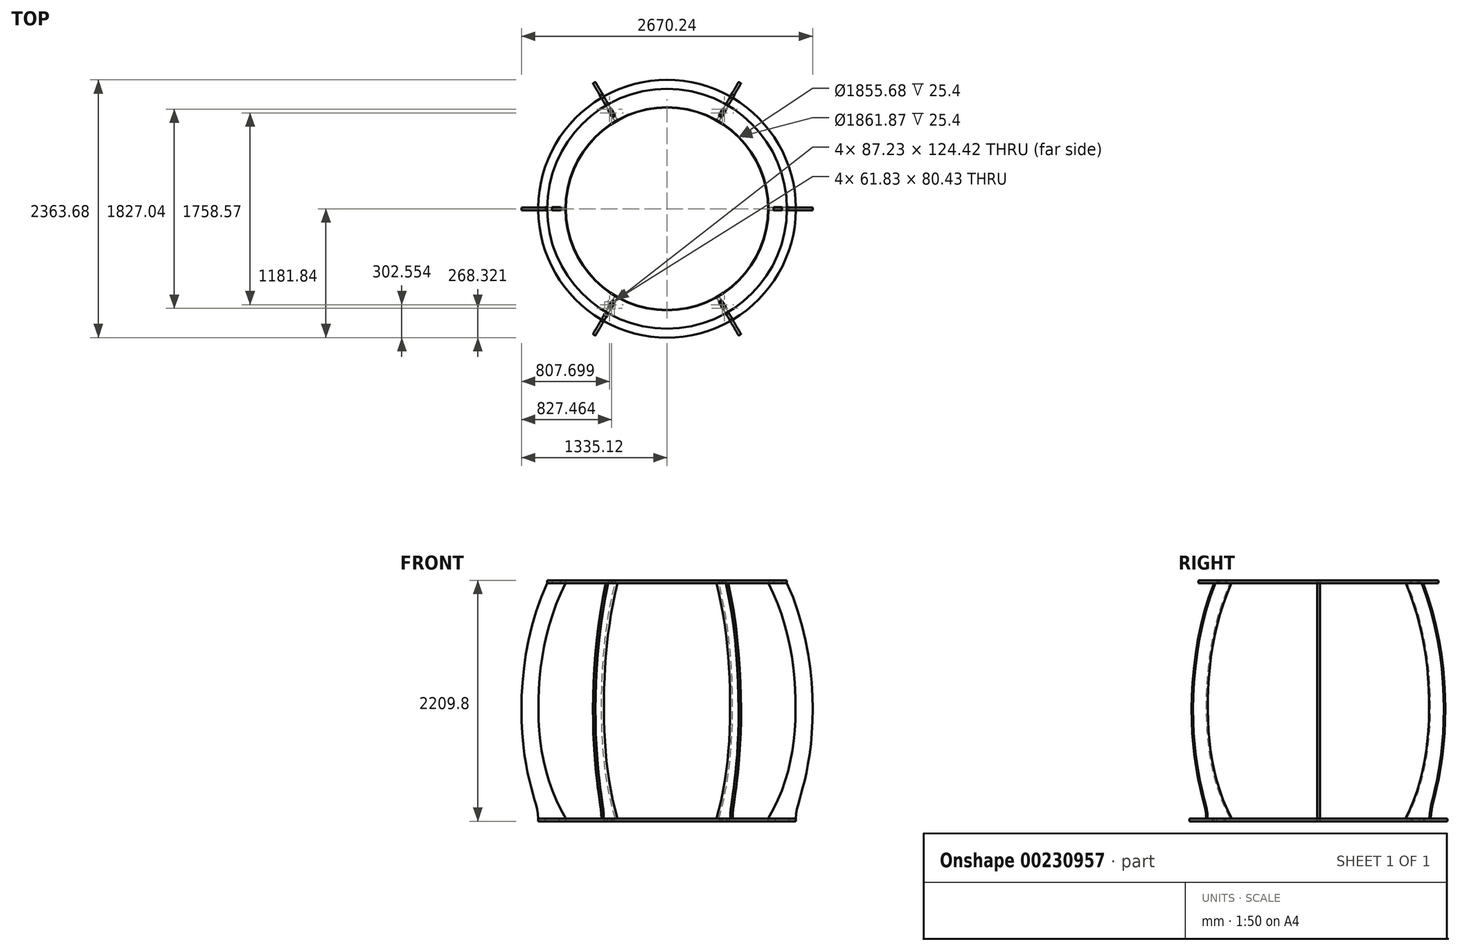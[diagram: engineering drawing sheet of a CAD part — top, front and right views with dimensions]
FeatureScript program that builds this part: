
annotation { "Feature Type Name" : "Feature", "Feature Type Description" : "" }
export const myFeature = defineFeature(function(context is Context, id is Id, definition is map)
    precondition{}
    {
        {
            var Q0;
            Q0=qCreatedBy(makeId("Front.planeOp"),FACE);
            var sketch = newSketch(context, id + "F0", { "sketchPlane" : qUnion([Q0])});
            skLineSegment(sketch, "E0", {"start": v(-1181.84, -1150.9) * mm, "end": v(-927.84, -1150.9) * mm});
            skFitSpline(sketch, "E1", {"points": [v(0, 1953.34) * mm, v(-1100.72, 1005.82) * mm, v(-1321.31, -446.03) * mm, v(-1216.83, -971.67) * mm, v(-1181.84, -1150.9) * mm], "startDerivative": vector(-4000.43, 5.06) * mm, "endDerivative": vector(0, -1489.55) * mm});
            skLineSegment(sketch, "E2", {"start": v(-1099.69, 1008.1) * mm, "end": v(-930.94, 1008.1) * mm});
            skLineSegment(sketch, "E3", {"start": v(-1181.84, -1150.9) * mm, "end": v(-1181.84, -1354.1) * mm});
            skLineSegment(sketch, "E4", {"start": v(-1181.84, -1354.1) * mm, "end": v(-877.04, -1354.1) * mm});
            skLineSegment(sketch, "E5", {"start": v(-877.04, -1354.1) * mm, "end": v(-877.04, -1252.5) * mm});
            skLineSegment(sketch, "E6", {"start": v(-877.04, -1252.5) * mm, "end": v(-927.84, -1252.5) * mm});
            skLineSegment(sketch, "E7", {"start": v(-927.84, -1252.5) * mm, "end": v(-927.84, -1150.9) * mm});
            skFitSpline(sketch, "E8.trimOffspring", {"points": [v(0, -1757.92) * mm, v(-927.84, -1150.9) * mm, v(-1179.31, -127.8) * mm, v(-917.89, 1034.08) * mm, v(0, 1800.66) * mm], "startDerivative": vector(-4973.2, 113.59) * mm, "endDerivative": vector(4756.7, 336.76) * mm});
            skLineSegment(sketch, "E9", {"start": v(-1023.33, 1160.5) * mm, "end": v(-848.12, 1160.5) * mm});
            skLineSegment(sketch, "E10", {"start": v(0, 1953.34) * mm, "end": v(0, 1800.66) * mm});
            skLineSegment(sketch, "E11.bottom", {"start": v(-1118.34, -1125.5) * mm, "end": v(-991.34, -1125.5) * mm});
            skLineSegment(sketch, "E11.top", {"start": v(-1118.34, -1176.3) * mm, "end": v(-991.34, -1176.3) * mm});
            skLineSegment(sketch, "E11.left", {"start": v(-1118.34, -1125.5) * mm, "end": v(-1118.34, -1176.3) * mm});
            skLineSegment(sketch, "E11.right", {"start": v(-991.34, -1125.5) * mm, "end": v(-991.34, -1176.3) * mm});
            skPoint(sketch, "E11.middle", {"position": v(-1054.84, -1150.9) * mm});
            skLineSegment(sketch, "E12.bottom", {"start": v(-1053.41, 1033.5) * mm, "end": v(-977.21, 1033.5) * mm});
            skLineSegment(sketch, "E12.top", {"start": v(-1053.41, 982.7) * mm, "end": v(-977.21, 982.7) * mm});
            skLineSegment(sketch, "E12.left", {"start": v(-1053.41, 1033.5) * mm, "end": v(-1053.41, 982.7) * mm});
            skLineSegment(sketch, "E12.right", {"start": v(-977.21, 1033.5) * mm, "end": v(-977.21, 982.7) * mm});
            skPoint(sketch, "E12.middle", {"position": v(-1015.31, 1008.1) * mm});
            skSolve(sketch);
        }
        {
            var Q0;
            {var subQ0=sQuery(id+"F0.wireOp",EDGE,"E0");Q0=makeQuery(id+"F0.imprint","IMPRINT",FACE,{"disambiguationData":[TD([[makeQuery(id+"F0.imprint","IMPRINT",EDGE,{"derivedFrom":subQ0}),1.0]])]});}
            var Q1;
            {var subQ5=sQuery(id+"F0.wireOp",EDGE,"E12.top");Q1=makeQuery(id+"F0.imprint","IMPRINT",FACE,{"disambiguationData":[TD([[makeQuery(id+"F0.imprint","IMPRINT",EDGE,{"derivedFrom":subQ5}),1.0]])]});}
            var Q2;
            {var subQ5=sQuery(id+"F0.wireOp",EDGE,"E12.bottom");Q2=makeQuery(id+"F0.imprint","IMPRINT",FACE,{"disambiguationData":[TD([[makeQuery(id+"F0.imprint","IMPRINT",EDGE,{"derivedFrom":subQ5}),-1.0]])]});}
            var Q3;
            {var subQ5=sQuery(id+"F0.wireOp",EDGE,"E11.bottom");Q3=makeQuery(id+"F0.imprint","IMPRINT",FACE,{"disambiguationData":[TD([[makeQuery(id+"F0.imprint","IMPRINT",EDGE,{"derivedFrom":subQ5}),-1.0]])]});}
            var Q4;
            {var subQ5=sQuery(id+"F0.wireOp",EDGE,"E11.top");Q4=makeQuery(id+"F0.imprint","IMPRINT",FACE,{"disambiguationData":[TD([[makeQuery(id+"F0.imprint","IMPRINT",EDGE,{"derivedFrom":subQ5}),1.0]])]});}
            extrude(context, id + "F1", {"entities" : qUnion([Q0, Q1, Q2, Q3, Q4]), "endBound" : BoundingType.SYMMETRIC, "depth" : 25.4 * mm});
        }
        {
            var Q0;
            Q0=makeQuery(id+"F1.opExtrude","SWEPT_BODY",BODY,{"disambiguationData":[OSD([sQuery(id+"F0.wireOp",EDGE,"E0"),sQuery(id+"F0.wireOp",EDGE,"E1"),sQuery(id+"F0.wireOp",EDGE,"E2"),sQuery(id+"F0.wireOp",EDGE,"E8.trimOffspring")])]});
            var Q1;
            Q1=sQuery(id+"F0.wireOp",EDGE,"E10");
            circularPattern(context, id + "F2", {"entities" : qUnion([Q0]), "axis" : qUnion([Q1]), "angle" : 360 * degree, "instanceCount" : 6, "equalSpace" : true});
        }
        {
            var Q0;
            Q0=qCreatedBy(makeId("Top.planeOp"),FACE);
            var Q1;
            Q1=sQuery(id+"F0.wireOp",VERTEX,"E8.trimOffspring.1.internal");
            cPlane(context, id + "F3", {"entities" : qUnion([Q0, Q1]), "cplaneType" : CPlaneType.PLANE_POINT, "offset" : 25.4 * mm, "width" : 152.4 * mm, "height" : 152.4 * mm});
        }
        {
            var Q0;
            Q0=qCreatedBy(id+"F3.planeOp",FACE);
            var sketch = newSketch(context, id + "F4", { "sketchPlane" : qUnion([Q0])});
            skCircle(sketch, "E13", {"center": v(0, 0) * mm, "radius": 1181.84 * mm});
            skCircle(sketch, "E14", {"center": v(0, 0) * mm, "radius": 927.84 * mm});
            skLineSegment(sketch, "E15.bottom", {"start": v(-1118.98, 13.33) * mm, "end": v(-990.7, 13.33) * mm});
            skLineSegment(sketch, "E15.top", {"start": v(-1118.98, -13.34) * mm, "end": v(-990.7, -13.34) * mm});
            skLineSegment(sketch, "E15.left", {"start": v(-1118.98, 13.33) * mm, "end": v(-1118.98, -13.34) * mm});
            skLineSegment(sketch, "E15.right", {"start": v(-990.7, 13.33) * mm, "end": v(-990.7, -13.34) * mm});
            skPoint(sketch, "E15.middle", {"position": v(-1054.84, 0) * mm});
            skLineSegment(sketch, "E16.1.0", {"start": v(-571.04, -962.4) * mm, "end": v(-506.9, -851.3) * mm});
            skLineSegment(sketch, "E16.1.1", {"start": v(-571.04, -962.4) * mm, "end": v(-547.94, -975.73) * mm});
            skLineSegment(sketch, "E16.1.2", {"start": v(-547.94, -975.73) * mm, "end": v(-483.8, -864.64) * mm});
            skLineSegment(sketch, "E16.1.3", {"start": v(-506.9, -851.3) * mm, "end": v(-483.8, -864.64) * mm});
            skLineSegment(sketch, "E16.2.0", {"start": v(547.94, -975.73) * mm, "end": v(483.8, -864.64) * mm});
            skLineSegment(sketch, "E16.2.1", {"start": v(547.94, -975.73) * mm, "end": v(571.04, -962.4) * mm});
            skLineSegment(sketch, "E16.2.2", {"start": v(571.04, -962.4) * mm, "end": v(506.9, -851.3) * mm});
            skLineSegment(sketch, "E16.2.3", {"start": v(483.8, -864.64) * mm, "end": v(506.9, -851.3) * mm});
            skLineSegment(sketch, "E16.3.0", {"start": v(1118.98, -13.33) * mm, "end": v(990.7, -13.33) * mm});
            skLineSegment(sketch, "E16.3.1", {"start": v(1118.98, -13.33) * mm, "end": v(1118.98, 13.34) * mm});
            skLineSegment(sketch, "E16.3.2", {"start": v(1118.98, 13.34) * mm, "end": v(990.7, 13.34) * mm});
            skLineSegment(sketch, "E16.3.3", {"start": v(990.7, -13.33) * mm, "end": v(990.7, 13.34) * mm});
            skLineSegment(sketch, "E16.4.0", {"start": v(571.04, 962.4) * mm, "end": v(506.9, 851.3) * mm});
            skLineSegment(sketch, "E16.4.1", {"start": v(571.04, 962.4) * mm, "end": v(547.94, 975.73) * mm});
            skLineSegment(sketch, "E16.4.2", {"start": v(547.94, 975.73) * mm, "end": v(483.8, 864.64) * mm});
            skLineSegment(sketch, "E16.4.3", {"start": v(506.9, 851.3) * mm, "end": v(483.8, 864.64) * mm});
            skLineSegment(sketch, "E16.5.0", {"start": v(-547.94, 975.73) * mm, "end": v(-483.8, 864.64) * mm});
            skLineSegment(sketch, "E16.5.1", {"start": v(-547.94, 975.73) * mm, "end": v(-571.04, 962.4) * mm});
            skLineSegment(sketch, "E16.5.2", {"start": v(-571.04, 962.4) * mm, "end": v(-506.9, 851.3) * mm});
            skLineSegment(sketch, "E16.5.3", {"start": v(-483.8, 864.64) * mm, "end": v(-506.9, 851.3) * mm});
            skSolve(sketch);
        }
        {
            var Q0;
            Q0=makeQuery(id+"F4.imprint","IMPRINT",FACE,{"disambiguationData":[TD([[makeQuery(id+"F4.imprint","IMPRINT",EDGE,{"derivedFrom":sQuery(id+"F4.wireOp",EDGE,"E13")}),1.0]])]});
            extrude(context, id + "F5", {"entities" : qUnion([Q0]), "oppositeDirection" : true, "depth" : 25.4 * mm});
        }
        {
            var Q0;
            Q0=qCreatedBy(makeId("Top.planeOp"),FACE);
            var Q1;
            Q1=sQuery(id+"F0.wireOp",VERTEX,"E2.end");
            cPlane(context, id + "F6", {"entities" : qUnion([Q0, Q1]), "cplaneType" : CPlaneType.PLANE_POINT, "offset" : 25.4 * mm, "width" : 152.4 * mm, "height" : 152.4 * mm});
        }
        {
            var Q0;
            Q0=qCreatedBy(id+"F6.planeOp",FACE);
            var sketch = newSketch(context, id + "F7", { "sketchPlane" : qUnion([Q0])});
            skCircle(sketch, "E17", {"center": v(0, 0) * mm, "radius": 1099.69 * mm});
            skCircle(sketch, "E18", {"center": v(0, 0) * mm, "radius": 930.94 * mm});
            skLineSegment(sketch, "E19.bottom", {"start": v(-1054.05, 13.33) * mm, "end": v(-976.58, 13.33) * mm});
            skLineSegment(sketch, "E19.top", {"start": v(-1054.05, -13.34) * mm, "end": v(-976.58, -13.34) * mm});
            skLineSegment(sketch, "E19.left", {"start": v(-1054.05, 13.33) * mm, "end": v(-1054.05, -13.34) * mm});
            skLineSegment(sketch, "E19.right", {"start": v(-976.58, 13.33) * mm, "end": v(-976.58, -13.34) * mm});
            skPoint(sketch, "E19.middle", {"position": v(-1015.31, 0) * mm});
            skLineSegment(sketch, "E20.1.0", {"start": v(-538.57, -906.16) * mm, "end": v(-499.84, -839.07) * mm});
            skLineSegment(sketch, "E20.1.1", {"start": v(-538.57, -906.16) * mm, "end": v(-515.48, -919.5) * mm});
            skLineSegment(sketch, "E20.1.2", {"start": v(-515.48, -919.5) * mm, "end": v(-476.74, -852.4) * mm});
            skLineSegment(sketch, "E20.1.3", {"start": v(-499.84, -839.07) * mm, "end": v(-476.74, -852.4) * mm});
            skLineSegment(sketch, "E20.2.0", {"start": v(515.48, -919.5) * mm, "end": v(476.74, -852.4) * mm});
            skLineSegment(sketch, "E20.2.1", {"start": v(515.48, -919.5) * mm, "end": v(538.57, -906.16) * mm});
            skLineSegment(sketch, "E20.2.2", {"start": v(538.57, -906.16) * mm, "end": v(499.84, -839.07) * mm});
            skLineSegment(sketch, "E20.2.3", {"start": v(476.74, -852.4) * mm, "end": v(499.84, -839.07) * mm});
            skLineSegment(sketch, "E20.3.0", {"start": v(1054.05, -13.34) * mm, "end": v(976.58, -13.34) * mm});
            skLineSegment(sketch, "E20.3.1", {"start": v(1054.05, -13.34) * mm, "end": v(1054.05, 13.33) * mm});
            skLineSegment(sketch, "E20.3.2", {"start": v(1054.05, 13.33) * mm, "end": v(976.58, 13.33) * mm});
            skLineSegment(sketch, "E20.3.3", {"start": v(976.58, -13.34) * mm, "end": v(976.58, 13.33) * mm});
            skLineSegment(sketch, "E20.4.0", {"start": v(538.57, 906.16) * mm, "end": v(499.84, 839.07) * mm});
            skLineSegment(sketch, "E20.4.1", {"start": v(538.57, 906.16) * mm, "end": v(515.48, 919.5) * mm});
            skLineSegment(sketch, "E20.4.2", {"start": v(515.48, 919.5) * mm, "end": v(476.74, 852.4) * mm});
            skLineSegment(sketch, "E20.4.3", {"start": v(499.84, 839.07) * mm, "end": v(476.74, 852.4) * mm});
            skLineSegment(sketch, "E20.5.0", {"start": v(-515.48, 919.5) * mm, "end": v(-476.74, 852.4) * mm});
            skLineSegment(sketch, "E20.5.1", {"start": v(-515.48, 919.5) * mm, "end": v(-538.57, 906.16) * mm});
            skLineSegment(sketch, "E20.5.2", {"start": v(-538.57, 906.16) * mm, "end": v(-499.84, 839.07) * mm});
            skLineSegment(sketch, "E20.5.3", {"start": v(-476.74, 852.4) * mm, "end": v(-499.84, 839.07) * mm});
            skSolve(sketch);
        }
        {
            var Q0;
            Q0=makeQuery(id+"F7.imprint","IMPRINT",FACE,{"disambiguationData":[TD([[makeQuery(id+"F7.imprint","IMPRINT",EDGE,{"derivedFrom":sQuery(id+"F7.wireOp",EDGE,"E17")}),1.0]])]});
            extrude(context, id + "F8", {"entities" : qUnion([Q0]), "depth" : 25.4 * mm});
        }
    });
